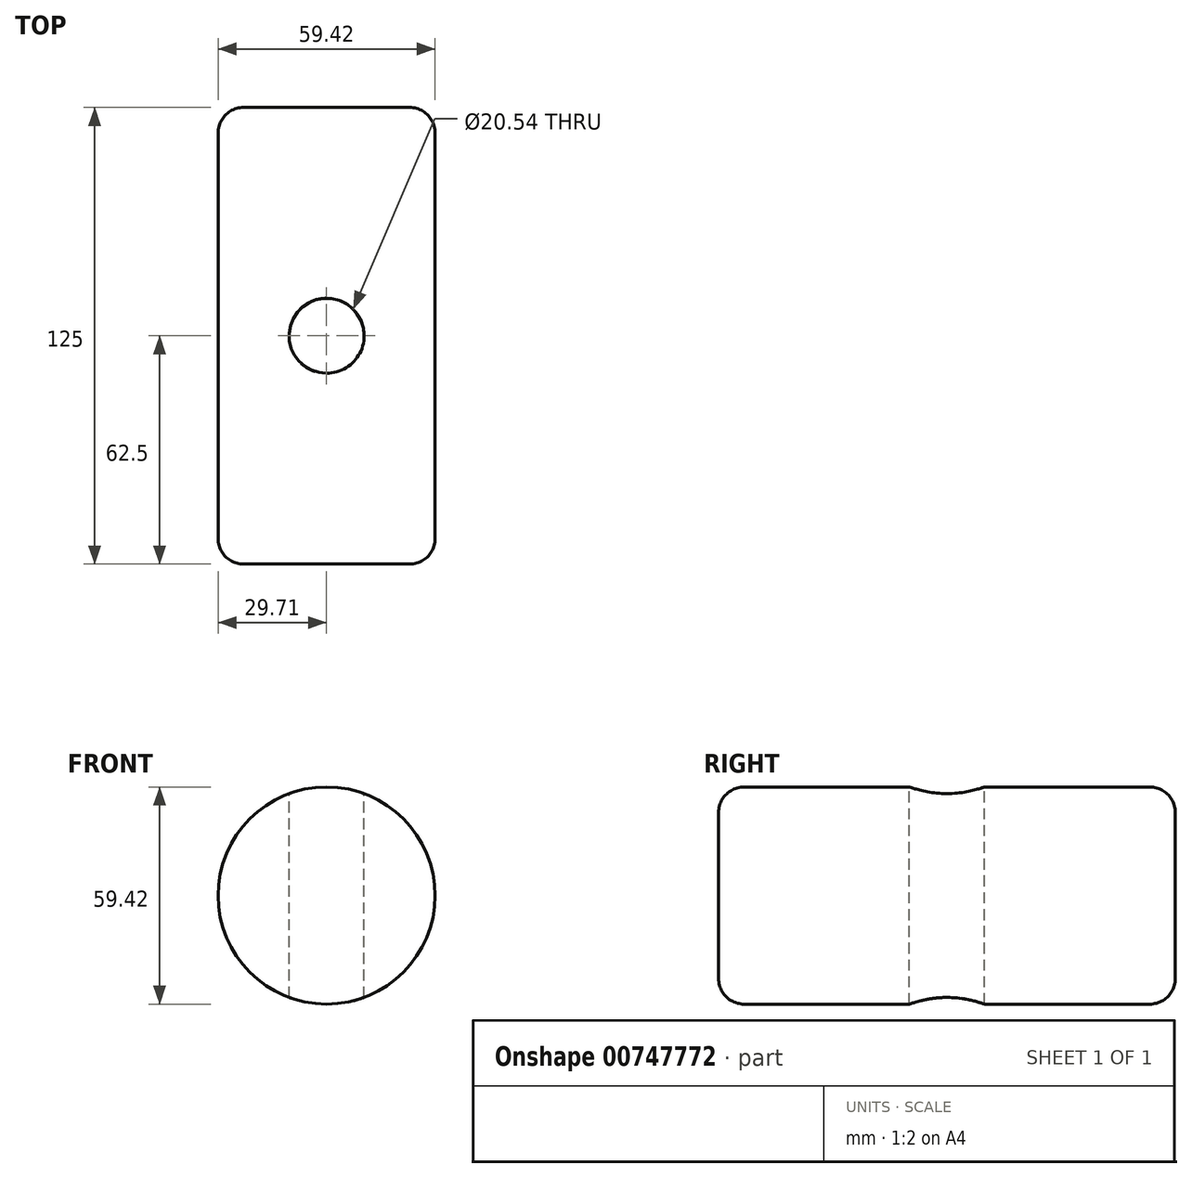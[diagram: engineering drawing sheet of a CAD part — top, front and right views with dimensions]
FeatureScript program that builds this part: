
annotation { "Feature Type Name" : "Feature", "Feature Type Description" : "" }
export const myFeature = defineFeature(function(context is Context, id is Id, definition is map)
    precondition{}
    {
        {
            var Q0;
            Q0=qCreatedBy(makeId("Front.planeOp"),FACE);
            var sketch = newSketch(context, id + "F0", { "sketchPlane" : qUnion([Q0])});
            skCircle(sketch, "E0", {"center": v(0, 0) * mm, "radius": 29.71 * mm});
            skSolve(sketch);
        }
        {
            var Q0;
            Q0 = qSketchRegion(id + "F0", true);
            extrude(context, id + "F1", {"entities" : qUnion([Q0]), "endBound" : BoundingType.SYMMETRIC, "depth" : 125 * mm, "offsetDistance" : 25 * mm});
        }
        {
            var Q0;
            Q0=qCreatedBy(makeId("Top.planeOp"),FACE);
            var sketch = newSketch(context, id + "F2", { "sketchPlane" : qUnion([Q0])});
            skCircle(sketch, "E1", {"center": v(0, 0) * mm, "radius": 10.27 * mm});
            skSolve(sketch);
        }
        {
            var Q0;
            Q0 = qSketchRegion(id + "F2", true);
            extrude(context, id + "F3", {"entities" : qUnion([Q0]), "operationType" : NewBodyOperationType.REMOVE, "endBound" : BoundingType.SYMMETRIC, "oppositeDirection" : true, "depth" : 80 * mm, "offsetDistance" : 25 * mm});
        }
        {
            var Q0;
            Q0=makeQuery(id+"F1.opExtrude","CAP_FACE",FACE,{"disambiguationData":[OSD([sQuery(id+"F0.wireOp",EDGE,"E0")])],"isStart":false});
            var Q1;
            Q1=makeQuery(id+"F1.opExtrude","CAP_FACE",FACE,{"disambiguationData":[OSD([sQuery(id+"F0.wireOp",EDGE,"E0")])],"isStart":true});
            fillet(context, id + "F4", {"entities" : qUnion([Q0, Q1]), "radius" : 7 * mm, "tangentPropagation" : true, "allowEdgeOverflow" : false});
        }
    });
